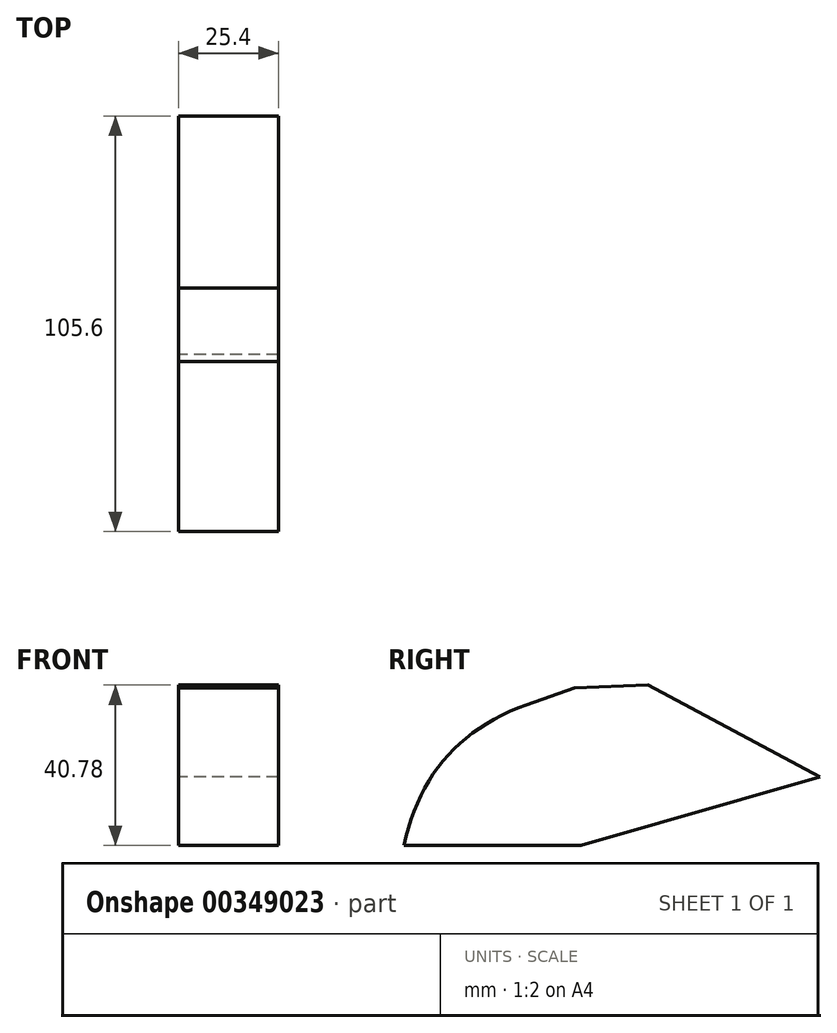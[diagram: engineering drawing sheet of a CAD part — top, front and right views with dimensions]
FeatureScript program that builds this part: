
annotation { "Feature Type Name" : "Feature", "Feature Type Description" : "" }
export const myFeature = defineFeature(function(context is Context, id is Id, definition is map)
    precondition{}
    {
        {
            var Q0;
            Q0=qCreatedBy(makeId("Right.planeOp"),FACE);
            var sketch = newSketch(context, id + "F0", { "sketchPlane" : qUnion([Q0])});
            skLineSegment(sketch, "E0", {"start": v(0, 0) * mm, "end": v(-44.93, 0) * mm});
            skLineSegment(sketch, "E1", {"start": v(-44.93, 0) * mm, "end": v(-54.04, 21.42) * mm});
            skLineSegment(sketch, "E2", {"start": v(-54.04, 21.42) * mm, "end": v(10.24, 44.37) * mm});
            skLineSegment(sketch, "E3", {"start": v(10.24, 44.37) * mm, "end": v(60.67, 17.44) * mm});
            skLineSegment(sketch, "E4", {"start": v(60.67, 17.44) * mm, "end": v(0, 0) * mm});
            skSolve(sketch);
        }
        {
            var Q0;
            Q0=makeQuery(id+"F0.imprint","IMPRINT",FACE,{"disambiguationData":[TD([[makeQuery(id+"F0.imprint","IMPRINT",EDGE,{"derivedFrom":sQuery(id+"F0.wireOp",EDGE,"E0")}),-1.0]])]});
            extrude(context, id + "F1", {"entities" : qUnion([Q0]), "depth" : 25.4 * mm});
        }
        {
            var Q0;
            Q0=makeQuery(id+"F1.opExtrude","SWEPT_EDGE",EDGE,{"disambiguationData":[OSD([sQuery(id+"F0.wireOp",EDGE,"E1"),sQuery(id+"F0.wireOp",EDGE,"E2")])]});
            fillet(context, id + "F2", {"entities" : qUnion([Q0]), "radius" : 48.28 * mm, "tangentPropagation" : true, "rho" : .5, "crossSection" : FilletCrossSection.CONIC, "allowEdgeOverflow" : false});
        }
        {
            var Q0;
            Q0=makeQuery(id+"F1.opExtrude","SWEPT_EDGE",EDGE,{"disambiguationData":[OSD([sQuery(id+"F0.wireOp",EDGE,"E2"),sQuery(id+"F0.wireOp",EDGE,"E3")])]});
            chamfer(context, id + "F3", {"entities" : qUnion([Q0]), "chamferType" : ChamferType.TWO_OFFSETS, "width1" : 12.7 * mm, "oppositeDirection" : false, "width2" : 7.62 * mm, "tangentPropagation" : true});
        }
    });
